# Revit family: Accessory-Flush_Actuator_Plate-KOHLER-Lynk-K-75890IN
name_source: partatom
category: Specialty Equipment
revit_build: Autodesk Revit 2017 (Build: 20160225_1515(x64)
units: mm (PartAtom-declared; Revit-internal decimal feet)

## family parameters
Cut with Voids When Loaded = No
Host = Face
OmniClass Number = 23.31.25.00
OmniClass Title = Toilet and Bath Specialties
Part Type = Normal
Room Calculation Point = No
Round Connector Dimension = Use Diameter
Shared = No

## types (5) — shared parameters
ADA Compliant = No
Assembly Code = C1030200
Date Modified = 01/08/2021
Default Elevation = 42"
Height = 6 5/16"
Length = 3/8"
Manufacturer = KOHLER Co.
Master Format 2014 = 10 28 00
Master Format 2014 Name = Toilet, Bath, and Laundry Accessories
Material = Plastic
Product Documentation Link = http://resources.kohler.com
Product Name = Lynk
Product Page URL = https://www.kohler.co.in
URL = https://www.kohler.co.in
WaterSense Certified = No
Width = 8 7/8"

## per-type parameters (varying)
| type | Description | Finish | Model | Type |
| Mechanical, CP- Polished Chrome | Faceplate for Instaflush Inwall Tank (Mechanical Operation) | KOHLER-Plastic-CP-Polished_Chrome | K-75890IN-M-CP | 1 |
| Mechanical, 0-White | Faceplate for Instaflush Inwall Tank (Mechanical Operation) | Kohler-Plastic-0-White | K-75890IN-M-0 | 2 |
| Mechanical, 7-Black Black | Faceplate for Instaflush Inwall Tank (Mechanical Operation) | Kohler-Plastic-7-Black_Black | K-75890IN-M-7 | 3 |
| Pneumatic, CP- Polished Chrome | Face Plate for Inwall Tank | KOHLER-Plastic-CP-Polished_Chrome | K-75890IN-P-CP | 4 |
| Pneumatic, BL-Matte Black | Face Plate for Inwall Tank | KOHLER-Plastic-BL-Matte_Black | K-75890IN-P-BL | 5 |

## geometry (parser evidence)
native form markers: Sweep x4
no freeform markers — native parametric forms only
